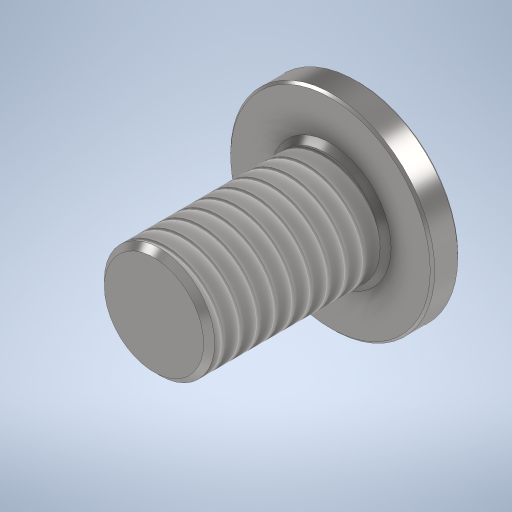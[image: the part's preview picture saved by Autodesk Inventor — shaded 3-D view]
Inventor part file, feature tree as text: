
AUTODESK INVENTOR PART (.ipt)
format: ipt  version: 2024 (Build 280153000, 153)  size: 368,640 bytes
history: native  units: mm
features: extrude x3, chamfer x3, sketch x2, thread x1, hole x1
ambient origin geometry x8: Origin, YZ Plane, XZ Plane, XY Plane, X Axis, Y Axis, Z Axis, Center Point
bodies: Solid1 (feature_tree)
feature tree (10):
  sketch  "Sketch1"  dims[d0=9.25mm d1=5.0mm]
  extrude  "Extrusion1"  Depth=5.0mm
  extrude  "Extrusion2"  Depth=2.5mm TaperAngle=0.0deg
  thread  "Thread1"  [1 undecoded]
  chamfer  "Chamfer1"  Distance=0.1mm Angle=45.0deg
  sketch  "Sketch2"  dims[d2=8.0mm d3=0.0mm d4=1.25mm d5=0.0mm d6=15.0mm d7=0.0mm d8=0.1mm d9=2.0mm d10=45.0deg d11=3.75mm d15=0.5mm d16=0.8mm d17=45.0deg d18=3.0mm d19=0.0mm d20=0.25mm d21=2.0mm d22=45.0deg d23=2.5mm d24=6.0mm d25=4.0mm d26=2.0mm d27=90.0deg d28=2.5mm d29=150.0deg d30=3.94mm d31=0.66mm d32=1.66mm d33=2.5mm]
  hole  "Hole1"  [1 undecoded]
  chamfer  "Chamfer2"  Distance=3.0mm
  extrude  "Extrusion4"  Depth=2.5mm TaperAngle=45.0deg
  chamfer  "Chamfer3"  Distance=2.5mm
note: 2 required parameter values undecoded (feature->parameter linkage not recoverable at this tier; creation-order binding heuristic only, values carry confidence <= 0.55)
